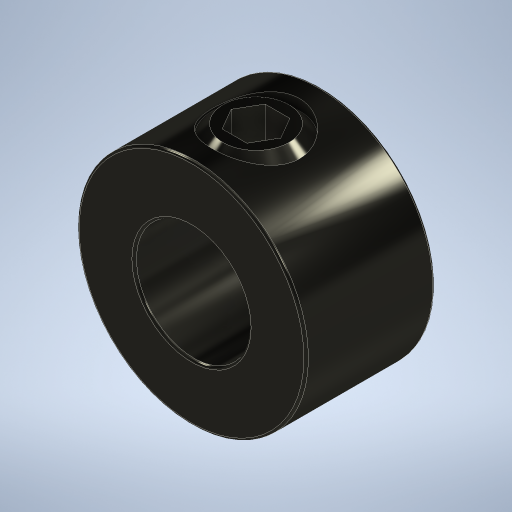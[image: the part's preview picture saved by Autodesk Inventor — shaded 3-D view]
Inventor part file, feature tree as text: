
AUTODESK INVENTOR PART (.ipt)
format: ipt  version: 2024 (Build 280153000, 153)  size: 295,424 bytes
history: native  units: in
note: dims shown in document units (in); Inventor stores cm internally (conversion verified against a paired STEP export)
features: fillet x1, other x1
ambient origin geometry x8: Origin, YZ Plane, XZ Plane, XY Plane, X Axis, Y Axis, Z Axis, Center Point
bodies: Solid1 (feature_tree), Solid2 (feature_tree)
feature tree (2):
  fillet  "Fillet1"  [1 undecoded]
  other  "Cut-Extrude2"
note: 1 required parameter value undecoded (feature->parameter linkage not recoverable at this tier; creation-order binding heuristic only, values carry confidence <= 0.55)
